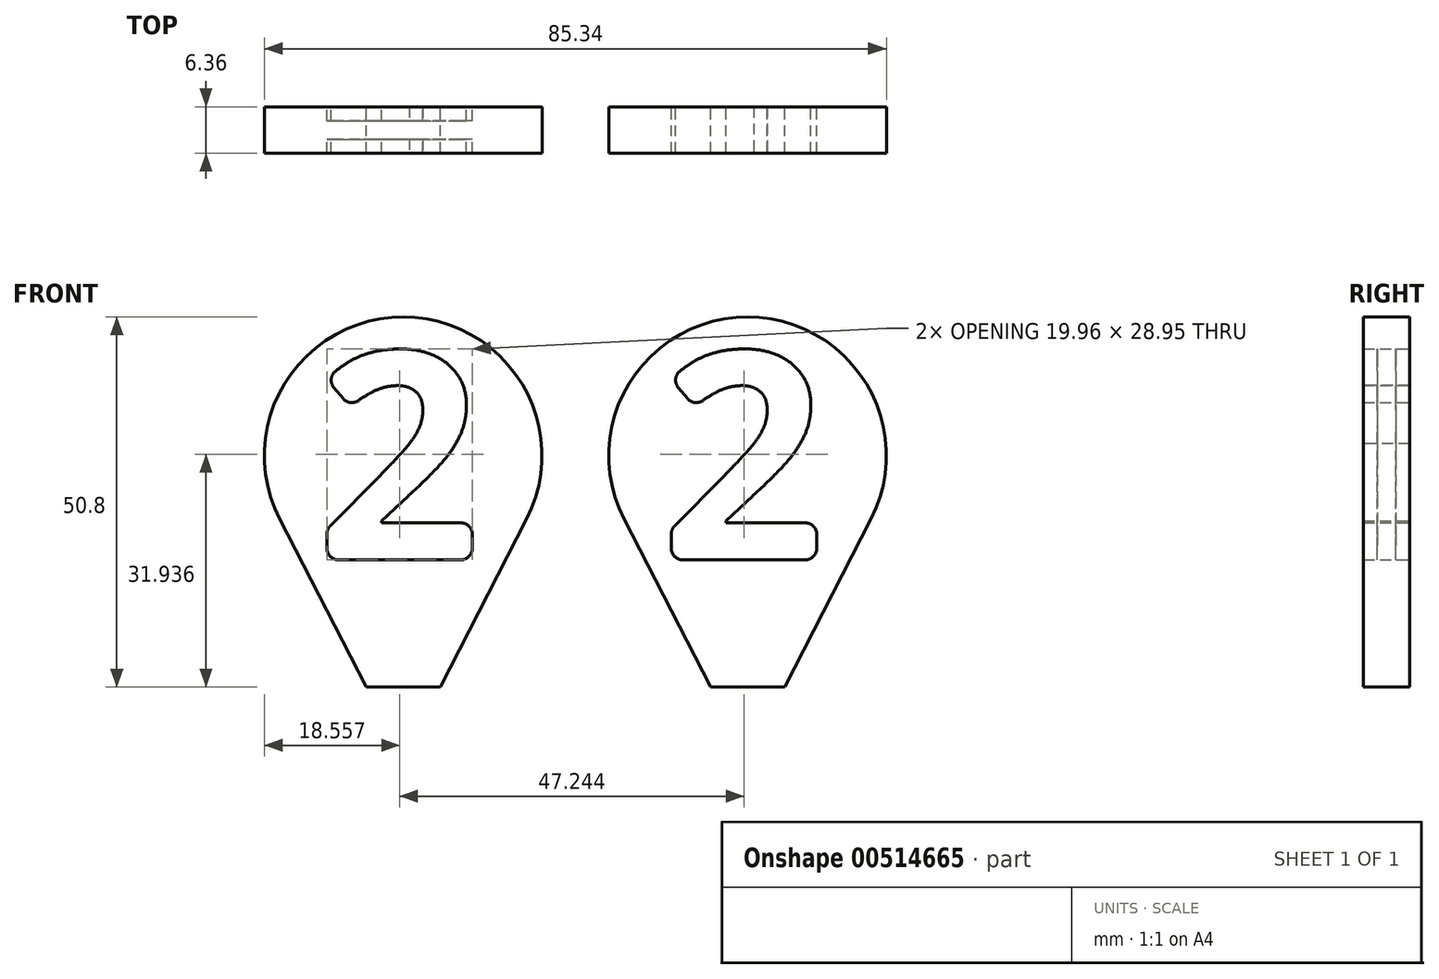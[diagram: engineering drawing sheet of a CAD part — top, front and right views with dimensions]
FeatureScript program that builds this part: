
annotation { "Feature Type Name" : "Feature", "Feature Type Description" : "" }
export const myFeature = defineFeature(function(context is Context, id is Id, definition is map)
    precondition{}
    {
        {
            var Q0;
            Q0=qCreatedBy(makeId("Front.planeOp"),FACE);
            var sketch = newSketch(context, id + "F0", { "sketchPlane" : qUnion([Q0])});
            skLineSegment(sketch, "E0", {"start": v(0, 0) * mm, "end": v(0, 50.8) * mm});
            skLineSegment(sketch, "E1", {"start": v(0, 0) * mm, "end": v(0, 31.75) * mm});
            skCircle(sketch, "E2", {"center": v(0, 31.75) * mm, "radius": 19.05 * mm});
            skLineSegment(sketch, "E3", {"start": v(0, 0) * mm, "end": v(5.08, 0) * mm});
            skLineSegment(sketch, "E4", {"start": v(0, 0) * mm, "end": v(-5.08, 0) * mm});
            skLineSegment(sketch, "E5", {"start": v(5.08, 0) * mm, "end": v(16.94, 23.03) * mm});
            skLineSegment(sketch, "E6", {"start": v(-5.08, 0) * mm, "end": v(-16.94, 23.03) * mm});
            skText(sketch, "E7", { "text": "2", "fontName": "OpenSans-Bold.ttf"});
            const initialGuessF0  = {"E7": [-0.01207, 0.01746, 1, 0, 0.02879]};
            skSetInitialGuess(sketch, initialGuessF0);
            skSolve(sketch);
        }
        {
            var Q0;
            {var subQ0=sQuery(id+"F0.wireOp",EDGE,"E7.sketch_text.stroke-1");Q0=makeQuery(id+"F0.imprint","IMPRINT",FACE,{"disambiguationData":[TD([[makeQuery(id+"F0.imprint","IMPRINT",EDGE,{"derivedFrom":subQ0}),1.0]])]});}
            var Q1;
            {var subQ0=sQuery(id+"F0.wireOp",EDGE,"E7.sketch_text.stroke-4");Q1=makeQuery(id+"F0.imprint","IMPRINT",FACE,{"disambiguationData":[TD([[makeQuery(id+"F0.imprint","IMPRINT",EDGE,{"derivedFrom":subQ0}),1.0]])]});}
            var Q2;
            {var subQ0=sQuery(id+"F0.wireOp",EDGE,"E7.sketch_text.stroke-15");Q2=makeQuery(id+"F0.imprint","IMPRINT",FACE,{"disambiguationData":[TD([[makeQuery(id+"F0.imprint","IMPRINT",EDGE,{"derivedFrom":subQ0}),1.0]])]});}
            var Q3;
            {var subQ0=sQuery(id+"F0.wireOp",EDGE,"E3");Q3=makeQuery(id+"F0.imprint","IMPRINT",FACE,{"disambiguationData":[TD([[makeQuery(id+"F0.imprint","IMPRINT",EDGE,{"derivedFrom":subQ0}),1.0]])]});}
            var Q4;
            {var subQ0=sQuery(id+"F0.wireOp",EDGE,"E4");Q4=makeQuery(id+"F0.imprint","IMPRINT",FACE,{"disambiguationData":[TD([[makeQuery(id+"F0.imprint","IMPRINT",EDGE,{"derivedFrom":subQ0}),-1.0]])]});}
            var Q5;
            {var subQ5=sQuery(id+"F0.wireOp",EDGE,"E7.sketch_text.stroke-21");Q5=makeQuery(id+"F0.imprint","IMPRINT",FACE,{"disambiguationData":[TD([[makeQuery(id+"F0.imprint","IMPRINT",EDGE,{"derivedFrom":subQ5}),1.0]])]});}
            extrude(context, id + "F1", {"entities" : qUnion([Q0, Q1, Q2, Q3, Q4, Q5]), "endBound" : BoundingType.SYMMETRIC, "depth" : 6.35 * mm, "offsetDistance" : 25.4 * mm});
        }
        {
            var Q0;
            Q0=makeQuery(id+"F1.opExtrude","SWEPT_EDGE",EDGE,{"disambiguationData":[OSD([sQuery(id+"F0.wireOp",EDGE,"E7.sketch_text.stroke-10"),sQuery(id+"F0.wireOp",EDGE,"E7.sketch_text.stroke-11")])]});
            var Q1;
            Q1=makeQuery(id+"F1.opExtrude","SWEPT_EDGE",EDGE,{"disambiguationData":[OSD([sQuery(id+"F0.wireOp",EDGE,"E7.sketch_text.stroke-9"),sQuery(id+"F0.wireOp",EDGE,"E7.sketch_text.stroke-10")])]});
            var Q2;
            Q2=makeQuery(id+"F1.opExtrude","SWEPT_EDGE",EDGE,{"disambiguationData":[OSD([sQuery(id+"F0.wireOp",EDGE,"E7.sketch_text.stroke-1"),sQuery(id+"F0.wireOp",EDGE,"E7.sketch_text.stroke-2")])]});
            var Q3;
            Q3=makeQuery(id+"F1.opExtrude","SWEPT_EDGE",EDGE,{"disambiguationData":[OSD([sQuery(id+"F0.wireOp",EDGE,"E7.sketch_text.stroke-0"),sQuery(id+"F0.wireOp",EDGE,"E7.sketch_text.stroke-1")])]});
            var Q4;
            Q4=makeQuery(id+"F1.opExtrude","SWEPT_EDGE",EDGE,{"disambiguationData":[OSD([sQuery(id+"F0.wireOp",EDGE,"E7.sketch_text.stroke-18"),sQuery(id+"F0.wireOp",EDGE,"E7.sketch_text.stroke-19")])]});
            var Q5;
            Q5=makeQuery(id+"F1.opExtrude","SWEPT_EDGE",EDGE,{"disambiguationData":[OSD([sQuery(id+"F0.wireOp",EDGE,"E7.sketch_text.stroke-0"),sQuery(id+"F0.wireOp",EDGE,"E7.sketch_text.stroke-19")])]});
            var Q6;
            Q6=makeQuery(id+"F1.opExtrude","SWEPT_EDGE",EDGE,{"disambiguationData":[OSD([sQuery(id+"F0.wireOp",EDGE,"E7.sketch_text.stroke-22"),sQuery(id+"F0.wireOp",EDGE,"E7.sketch_text.stroke-23")])]});
            fillet(context, id + "F2", {"entities" : qUnion([Q0, Q1, Q2, Q3, Q4, Q5, Q6]), "radius" : 1.59 * mm, "tangentPropagation" : true, "allowEdgeOverflow" : false});
        }
        {
            var Q0;
            Q0=makeQuery(id+"F1.opExtrude","SWEPT_BODY",BODY,{"disambiguationData":[OSD([sQuery(id+"F0.wireOp",EDGE,"E2"),sQuery(id+"F0.wireOp",EDGE,"E3"),sQuery(id+"F0.wireOp",EDGE,"E4"),sQuery(id+"F0.wireOp",EDGE,"E5"),sQuery(id+"F0.wireOp",EDGE,"E6"),sQuery(id+"F0.wireOp",EDGE,"E7.sketch_text.stroke-0"),sQuery(id+"F0.wireOp",EDGE,"E7.sketch_text.stroke-1"),sQuery(id+"F0.wireOp",EDGE,"E7.sketch_text.stroke-2"),sQuery(id+"F0.wireOp",EDGE,"E7.sketch_text.stroke-3"),sQuery(id+"F0.wireOp",EDGE,"E7.sketch_text.stroke-4"),sQuery(id+"F0.wireOp",EDGE,"E7.sketch_text.stroke-5"),sQuery(id+"F0.wireOp",EDGE,"E7.sketch_text.stroke-6"),sQuery(id+"F0.wireOp",EDGE,"E7.sketch_text.stroke-7"),sQuery(id+"F0.wireOp",EDGE,"E7.sketch_text.stroke-8"),sQuery(id+"F0.wireOp",EDGE,"E7.sketch_text.stroke-9"),sQuery(id+"F0.wireOp",EDGE,"E7.sketch_text.stroke-10"),sQuery(id+"F0.wireOp",EDGE,"E7.sketch_text.stroke-11"),sQuery(id+"F0.wireOp",EDGE,"E7.sketch_text.stroke-12"),sQuery(id+"F0.wireOp",EDGE,"E7.sketch_text.stroke-13"),sQuery(id+"F0.wireOp",EDGE,"E7.sketch_text.stroke-14"),sQuery(id+"F0.wireOp",EDGE,"E7.sketch_text.stroke-15"),sQuery(id+"F0.wireOp",EDGE,"E7.sketch_text.stroke-16"),sQuery(id+"F0.wireOp",EDGE,"E7.sketch_text.stroke-17"),sQuery(id+"F0.wireOp",EDGE,"E7.sketch_text.stroke-18"),sQuery(id+"F0.wireOp",EDGE,"E7.sketch_text.stroke-19"),sQuery(id+"F0.wireOp",EDGE,"E7.sketch_text.stroke-20"),sQuery(id+"F0.wireOp",EDGE,"E7.sketch_text.stroke-21"),sQuery(id+"F0.wireOp",EDGE,"E7.sketch_text.stroke-22"),sQuery(id+"F0.wireOp",EDGE,"E7.sketch_text.stroke-23")])]});
            transform(context, id + "F3", {"entities" : qUnion([Q0]), "transformType" : TransformType.TRANSLATION_3D, "dx" : 47.24 * mm, "dy" : 0 * mm, "dz" : 0 * mm, "makeCopy" : true});
        }
        {
            var Q0;
            {var subQ0=sQuery(id+"F0.wireOp",EDGE,"E7.sketch_text.stroke-8");Q0=makeQuery(id+"F0.imprint","IMPRINT",FACE,{"disambiguationData":[TD([[makeQuery(id+"F0.imprint","IMPRINT",EDGE,{"derivedFrom":subQ0}),-1.0]])]});}
            var Q1;
            {var subQ7=sQuery(id+"F0.wireOp",EDGE,"E7.sketch_text.stroke-4");Q1=makeQuery(id+"F0.imprint","IMPRINT",FACE,{"disambiguationData":[TD([[makeQuery(id+"F0.imprint","IMPRINT",EDGE,{"derivedFrom":subQ7}),-1.0]])]});}
            var Q2;
            {var subQ0=sQuery(id+"F0.wireOp",EDGE,"E7.sketch_text.stroke-1");Q2=makeQuery(id+"F0.imprint","IMPRINT",FACE,{"disambiguationData":[TD([[makeQuery(id+"F0.imprint","IMPRINT",EDGE,{"derivedFrom":subQ0}),-1.0]])]});}
            var Q3;
            {var subQ5=sQuery(id+"F0.wireOp",EDGE,"E7.sketch_text.stroke-23");Q3=makeQuery(id+"F0.imprint","IMPRINT",FACE,{"disambiguationData":[TD([[makeQuery(id+"F0.imprint","IMPRINT",EDGE,{"derivedFrom":subQ5}),-1.0]])]});}
            extrude(context, id + "F4", {"entities" : qUnion([Q0, Q1, Q2, Q3]), "operationType" : NewBodyOperationType.ADD, "endBound" : BoundingType.SYMMETRIC, "depth" : 2.54 * mm, "offsetDistance" : 25.4 * mm});
        }
    });
